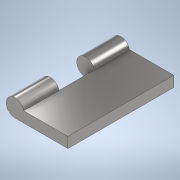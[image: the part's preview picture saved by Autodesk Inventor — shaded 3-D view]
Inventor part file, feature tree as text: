
AUTODESK INVENTOR PART (.ipt)
format: ipt  version: 2021 (Build 250183000, 183)  size: 114,176 bytes
history: native  units: mm
features: extrude x2, sketch x2, plane x1
ambient origin geometry x8: Origin, YZ Plane, XZ Plane, XY Plane, X Axis, Y Axis, Z Axis, Center Point
bodies: Solid1 (feature_tree)
feature tree (5):
  extrude  "Extrusion1"  Depth=30.0mm TaperAngle=0.0deg
  plane  "Work Plane1"
  extrude  "Extrusion2"  Depth=10.0mm
  sketch  "Sketch1"  dims[d0=15.0mm d1=3.0mm d2=5.0mm d3=30.0mm d4=0.0mm]
  sketch  "Sketch2"  dims[d5=-20.0mm d6=5.02mm d7=10.0mm d8=0.0mm]
